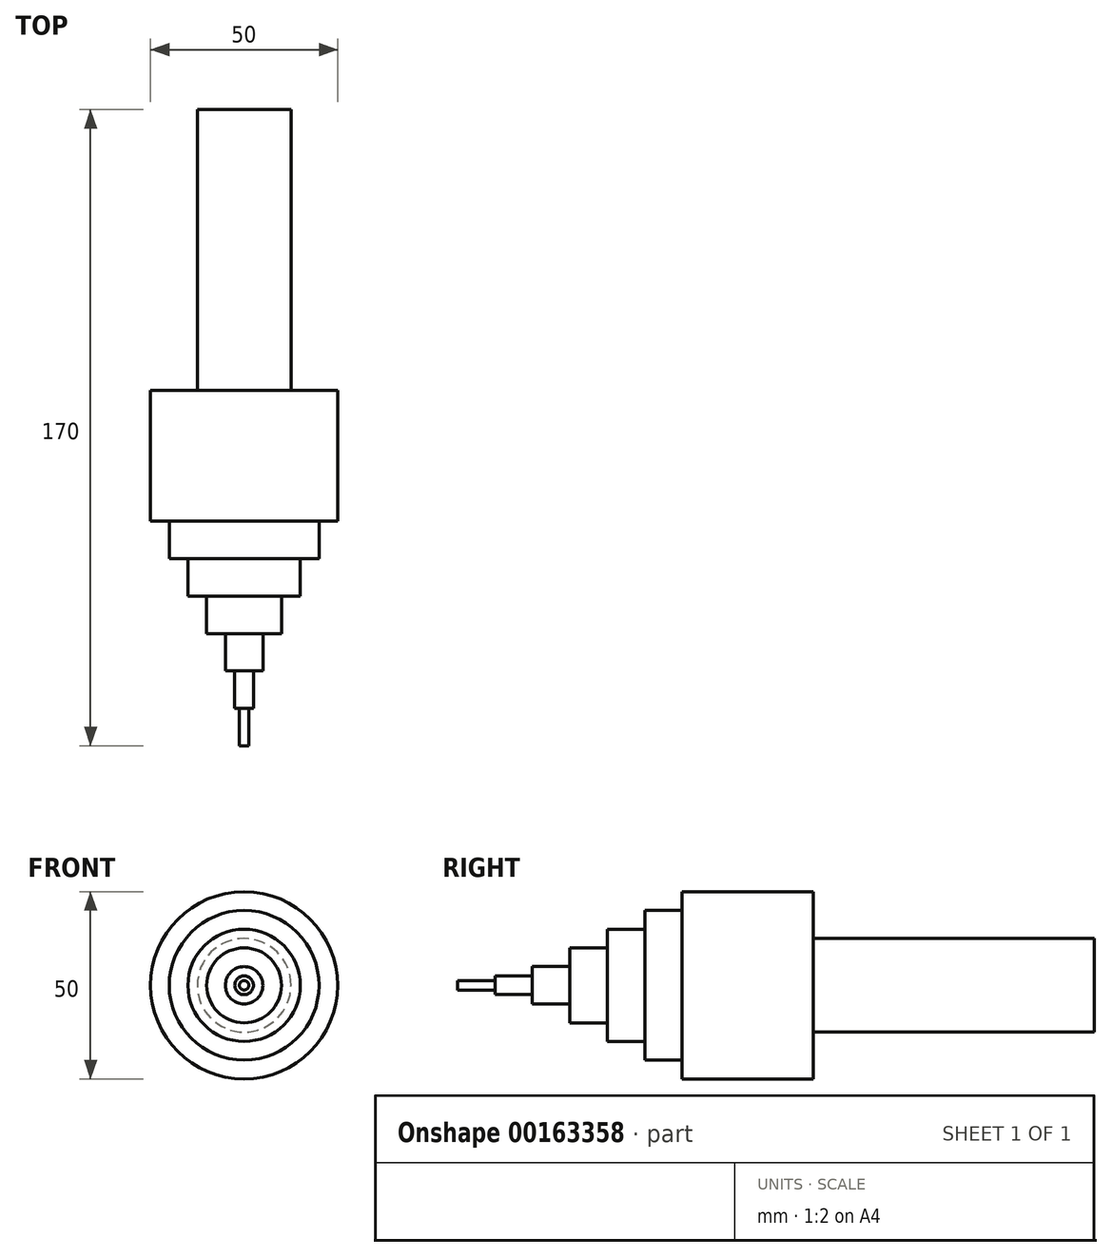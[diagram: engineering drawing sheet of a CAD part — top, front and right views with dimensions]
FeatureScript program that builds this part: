
annotation { "Feature Type Name" : "Feature", "Feature Type Description" : "" }
export const myFeature = defineFeature(function(context is Context, id is Id, definition is map)
    precondition{}
    {
        {
            var Q0;
            Q0=qCreatedBy(makeId("Front.planeOp"),FACE);
            var sketch = newSketch(context, id + "F0", { "sketchPlane" : qUnion([Q0])});
            skCircle(sketch, "E0", {"center": v(0, 0) * mm, "radius": 25 * mm});
            skSolve(sketch);
        }
        {
            var Q0;
            Q0=makeQuery(id+"F0.imprint","IMPRINT",FACE,{"disambiguationData":[TD([[makeQuery(id+"F0.imprint","IMPRINT",EDGE,{"derivedFrom":sQuery(id+"F0.wireOp",EDGE,"E0")}),1.0]])]});
            extrude(context, id + "F1", {"entities" : qUnion([Q0]), "endBound" : BoundingType.SYMMETRIC, "depth" : 25 * mm});
        }
        {
            var Q0;
            Q0=makeQuery(id+"F1.opExtrude","CAP_FACE",FACE,{"disambiguationData":[OSD([sQuery(id+"F0.wireOp",EDGE,"E0")])],"isStart":false});
            var sketch = newSketch(context, id + "F2", { "sketchPlane" : qUnion([Q0])});
            skCircle(sketch, "E1", {"center": v(0, 0) * mm, "radius": 5 * mm});
            skCircle(sketch, "E2", {"center": v(0, 0) * mm, "radius": 10 * mm});
            skCircle(sketch, "E3", {"center": v(0, 0) * mm, "radius": 15 * mm});
            skCircle(sketch, "E4", {"center": v(0, 0) * mm, "radius": 20 * mm});
            skCircle(sketch, "E5", {"center": v(0, 0) * mm, "radius": 2.5 * mm});
            skCircle(sketch, "E6", {"center": v(0, 0) * mm, "radius": 1.25 * mm});
            skSolve(sketch);
        }
        {
            var Q0;
            Q0=makeQuery(id+"F2.imprint","IMPRINT",FACE,{"disambiguationData":[TD([[makeQuery(id+"F2.imprint","IMPRINT",EDGE,{"derivedFrom":sQuery(id+"F2.wireOp",EDGE,"E1")}),1.0]])]});
            extrude(context, id + "F3", {"entities" : qUnion([Q0]), "operationType" : NewBodyOperationType.ADD, "depth" : 50 * mm});
        }
        {
            var Q0;
            Q0=makeQuery(id+"F2.imprint","IMPRINT",FACE,{"disambiguationData":[TD([[makeQuery(id+"F2.imprint","IMPRINT",EDGE,{"derivedFrom":sQuery(id+"F2.wireOp",EDGE,"E1")}),-1.0]])]});
            extrude(context, id + "F4", {"entities" : qUnion([Q0]), "operationType" : NewBodyOperationType.ADD, "depth" : 40 * mm});
        }
        {
            var Q0;
            Q0=makeQuery(id+"F2.imprint","IMPRINT",FACE,{"disambiguationData":[TD([[makeQuery(id+"F2.imprint","IMPRINT",EDGE,{"derivedFrom":sQuery(id+"F2.wireOp",EDGE,"E2")}),-1.0]])]});
            extrude(context, id + "F5", {"entities" : qUnion([Q0]), "operationType" : NewBodyOperationType.ADD, "depth" : 30 * mm});
        }
        {
            var Q0;
            Q0=makeQuery(id+"F2.imprint","IMPRINT",FACE,{"disambiguationData":[TD([[makeQuery(id+"F2.imprint","IMPRINT",EDGE,{"derivedFrom":sQuery(id+"F2.wireOp",EDGE,"E3")}),-1.0]])]});
            extrude(context, id + "F6", {"entities" : qUnion([Q0]), "operationType" : NewBodyOperationType.ADD, "depth" : 20 * mm});
        }
        {
            var Q0;
            Q0=makeQuery(id+"F2.imprint","IMPRINT",FACE,{"disambiguationData":[TD([[makeQuery(id+"F2.imprint","IMPRINT",EDGE,{"derivedFrom":sQuery(id+"F2.wireOp",EDGE,"E4")}),-1.0]])]});
            extrude(context, id + "F7", {"entities" : qUnion([Q0]), "operationType" : NewBodyOperationType.ADD, "depth" : 10 * mm});
        }
        {
            var Q0;
            Q0=makeQuery(id+"F2.imprint","IMPRINT",FACE,{"disambiguationData":[TD([[makeQuery(id+"F2.imprint","IMPRINT",EDGE,{"derivedFrom":sQuery(id+"F2.wireOp",EDGE,"E5")}),1.0]])]});
            extrude(context, id + "F8", {"entities" : qUnion([Q0]), "operationType" : NewBodyOperationType.ADD, "depth" : 60 * mm});
        }
        {
            var Q0;
            Q0=makeQuery(id+"F2.imprint","IMPRINT",FACE,{"disambiguationData":[TD([[makeQuery(id+"F2.imprint","IMPRINT",EDGE,{"derivedFrom":sQuery(id+"F2.wireOp",EDGE,"E6")}),1.0]])]});
            extrude(context, id + "F9", {"entities" : qUnion([Q0]), "operationType" : NewBodyOperationType.ADD, "depth" : 70 * mm});
        }
        {
            var Q0;
            Q0=makeQuery(id+"F1.opExtrude","CAP_FACE",FACE,{"disambiguationData":[OSD([sQuery(id+"F0.wireOp",EDGE,"E0")])],"isStart":true});
            var sketch = newSketch(context, id + "F10", { "sketchPlane" : qUnion([Q0])});
            skCircle(sketch, "E7", {"center": v(0, 0) * mm, "radius": 12.5 * mm});
            skSolve(sketch);
        }
        {
            var Q0;
            Q0=makeQuery(id+"F10.imprint","IMPRINT",FACE,{"disambiguationData":[TD([[makeQuery(id+"F10.imprint","IMPRINT",EDGE,{"derivedFrom":sQuery(id+"F10.wireOp",EDGE,"E7")}),1.0]])]});
            extrude(context, id + "F11", {"entities" : qUnion([Q0]), "operationType" : NewBodyOperationType.ADD, "depth" : 75 * mm});
        }
    });
